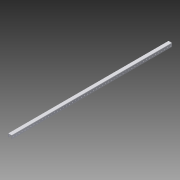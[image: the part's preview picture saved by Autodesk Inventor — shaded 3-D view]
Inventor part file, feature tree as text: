
AUTODESK INVENTOR PART (.ipt)
format: ipt  version: 2015 (Build 190159000, 159)  size: 468,992 bytes
history: native  units: in
note: dims shown in document units (in); Inventor stores cm internally (conversion verified against a paired STEP export)
features: extrude x2, sketch x2, pattern_linear x1
ambient origin geometry x8: Origin, YZ Plane, XZ Plane, XY Plane, X Axis, Y Axis, Z Axis, Center Point
bodies: Solid1 (feature_tree)
feature tree (5):
  extrude  "Extrusion1"  Depth=54.0in
  extrude  "Extrusion4"  Depth=0.5in
  pattern_linear  "Rectangular Pattern3"  Spacing1=0.5in  [1 undecoded]
  sketch  "Sketch1"  dims[d0=1.13in d1=1.25in d2=0.125in d3=0.125in d4=0.125in d5=54.0in]
  sketch  "Sketch4"  dims[d6=0.0in d34=0.5in d35=0.5in d36=0.25in d37=1.0in d38=0.0in d39=11.811in d41=1.0in d42=11.811in d44=1.0in]
note: 1 required parameter value undecoded (feature->parameter linkage not recoverable at this tier; creation-order binding heuristic only, values carry confidence <= 0.55)
